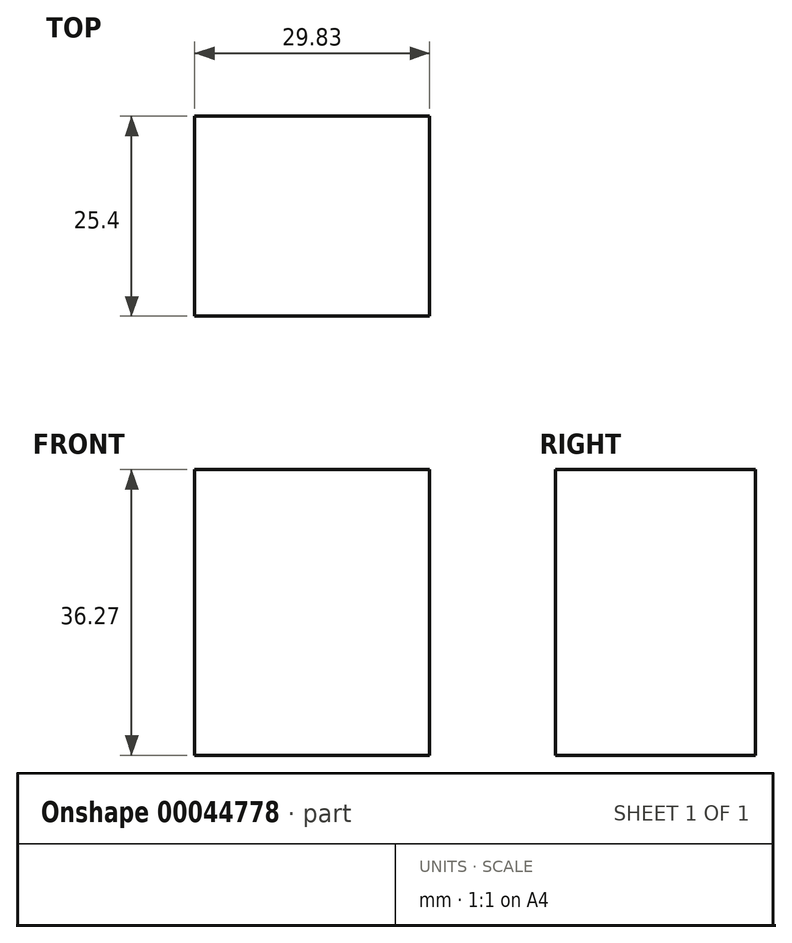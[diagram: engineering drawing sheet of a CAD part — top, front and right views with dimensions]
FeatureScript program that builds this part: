
annotation { "Feature Type Name" : "Feature", "Feature Type Description" : "" }
export const myFeature = defineFeature(function(context is Context, id is Id, definition is map)
    precondition{}
    {
        {
            var Q0;
            Q0=qCreatedBy(makeId("Front.planeOp"),FACE);
            var sketch = newSketch(context, id + "F0", { "sketchPlane" : qUnion([Q0])});
            skLineSegment(sketch, "E0.bottom", {"start": v(0, 0) * mm, "end": v(-29.83, 0) * mm});
            skLineSegment(sketch, "E0.top", {"start": v(0, -36.27) * mm, "end": v(-29.83, -36.27) * mm});
            skLineSegment(sketch, "E0.left", {"start": v(0, 0) * mm, "end": v(0, -36.27) * mm});
            skLineSegment(sketch, "E0.right", {"start": v(-29.83, 0) * mm, "end": v(-29.83, -36.27) * mm});
            skSolve(sketch);
        }
        {
            var Q0;
            Q0 = qSketchRegion(id + "F0", true);
            var Q1;
            Q1 = qSketchRegion(id + "FQdleLg12eYXhoi_0", true);
            extrude(context, id + "F1", {"entities" : qUnion([Q0, Q1]), "oppositeDirection" : true, "depth" : 25.4 * mm});
        }
    });
